# Revit family: WicStyle65Evo - 2 Leaf Inward Opening
name_source: partatom
category: Doors
revit_build: Autodesk Revit Architecture 2014 (Build: 20130308_1515(x64)
units: mm (PartAtom-declared; Revit-internal decimal feet)

## types (1)
- 1916002 + 1926510
    Acoustic = RA,tr = 35 dB
    Air Permeability = Class 4
    Analytic Construction = <None>
    Corrosion Resistance of the Fittings = NPD
    Date of publishing = 3/14/2015
    Description = Wicslide 65 sliding windows and patio doors is the perfect solution for combining high thermal performance and large sizes. With  its  various  designs  of  outer  and  opening  frames, multiple  leaf  combinations  (from  2  to  6  leaves)  and  its  comprehensive range of dual colour solutions, the Wicslide 65 brings greater freedom to building design. Designed  to  meet  market  demands,  Wicslide  65  sliding doors are perfectly suited for disabled access.
    Design country = Germany
    EN1627 Burglar Resistance = NPD
    Edition number = 1
    Frame 1916002 = Yes
    Frame 1916003 = No
    Frame 1916004 = No
    Frame 1926500 = No
    Frame 1926501 = No
    Frame 1926502 = No
    Frame Depth = 65 mm  [stored 0.213255 ft]
    Frame Material = WICONA - Aluminium - RAL7016 - Anthracite Grey - Matt
    Frame Projection Ext. = 25 mm  [stored 0.082021 ft]
    Frame Projection Int. = 25 mm  [stored 0.082021 ft]
    Frame Width = 58 mm  [stored 0.190289 ft]
    Frame Width 1 = 51 mm  [stored 0.167323 ft]
    Frame Width 2 = 36 mm
    Frame Width 3 = 26 mm  [stored 0.0853018 ft]
    FrameWarning = 1
    Function = Interior
    Glass Elevation = 9 mm  [stored 0.0295276 ft]
    Glass Offset Bottom = 129 mm
    Glass Thickness = 24 mm  [stored 0.0787402 ft]
    Glass offset side/top = 113 mm
    GlassLayer Thickness In = 5 mm  [stored 0.0164042 ft]
    GlassLayer Thickness Out = 5 mm  [stored 0.0164042 ft]
    Handle Height = 850 mm  [stored 2.78871 ft]
    Handle Material = Aluminium
    Handle Offset X = 30 mm  [stored 0.0984252 ft]
    Height = 2000 mm  [stored 6.56168 ft]
    Keynote = L10/330
    Leaf Height = 1923 mm  [stored 6.30906 ft]
    Leaf Material = WICONA - Aluminium - RAL7016 - Anthracite Grey - Matt
    Leaf Width 1 = 692 mm
    Leaf Width 2 = 667 mm  [stored 2.18832 ft]
    Load Bearing Capacity of Safety Devices = Fulfilled
    Main Leaf Width = 800 mm  [stored 2.62467 ft]
    Manufacturer = Wicona
    Manufacturer country = Germany
    Manufacturer name = Wicona
    Material main = Aluminium
    Material secondary = Glass
    Maximum Sash Weight = 150kg as standard design, heavier weights can easily be customised
    Mechanical Strength = Class 4
    Model = Wicslide 65 evo
    Nominal height = 210000
    Nominal width = 150000
    Opening Line Length 1 = 724 mm  [stored 2.37533 ft]
    Opening Line Length 1 Corse = 750 mm  [stored 2.46063 ft]
    Opening Line Length 2 = 724 mm  [stored 2.37533 ft]
    Opening Line Length 2 Corse = 750 mm  [stored 2.46063 ft]
    Operating Forces = Class 1
    Operation = IFC_DOORDBLSWING
    Product Guid = 1ef816c7-8b64-491b-b226-0f81c5fb437c
    Product SKU = WICSTYLE_65_EVO_D
    Product data url = http://bimobject.com
    Product family = Windows & Doors
    Product group = Windows
    QR code = http://bimobject.com
    Quality Assurance = Certified according to ISO 9001:2008
    Repeated Opening/Closing = Class 2 (10,000 Cycles)
    Rough Height = 1034 mm  [stored 3.39239 ft]
    Sash 1926510 = No
    Sash 1926511 = No
    Sash 1926512 = Yes
    Sash 1926535 = No
    Sash Bottom 1926516 = No
    Sash Bottom 1926517 = No
    Sash Bottom 1926518 = Yes
    SashBottomWarning = 1
    SashWarning = 1
    Symetrical Leafs = Yes
    Threshold 1926524 = No
    Threshold 1926525 = No
    Threshold 1926526 = No
    Threshold 3021033 = No
    Threshold 3926500 = No
    Threshold 3926502 = Yes
    Threshold Height = 21 mm  [stored 0.0688976 ft]
    Threshold Length = 1448 mm  [stored 4.75066 ft]
    Threshold Material = WICONA - Aluminium - RAL7016 - Anthracite Grey - Matt
    ThresholdWarning = 1
    URL = http://www.wicona.com
    Uniclass2 = Ss-25-30-95-28
    Wall Closure = By host
    WarningSign = No
    Watertightness = E900
    Weight Net (Kg) = 0
    Width = 1500 mm  [stored 4.92126 ft]

note: [stored X ft] marks values corroborated as IEEE doubles in the binary element streams (Revit-internal decimal feet)

## geometry (parser evidence)
native form markers: Blend x4, Sweep x30
no freeform markers — native parametric forms only
